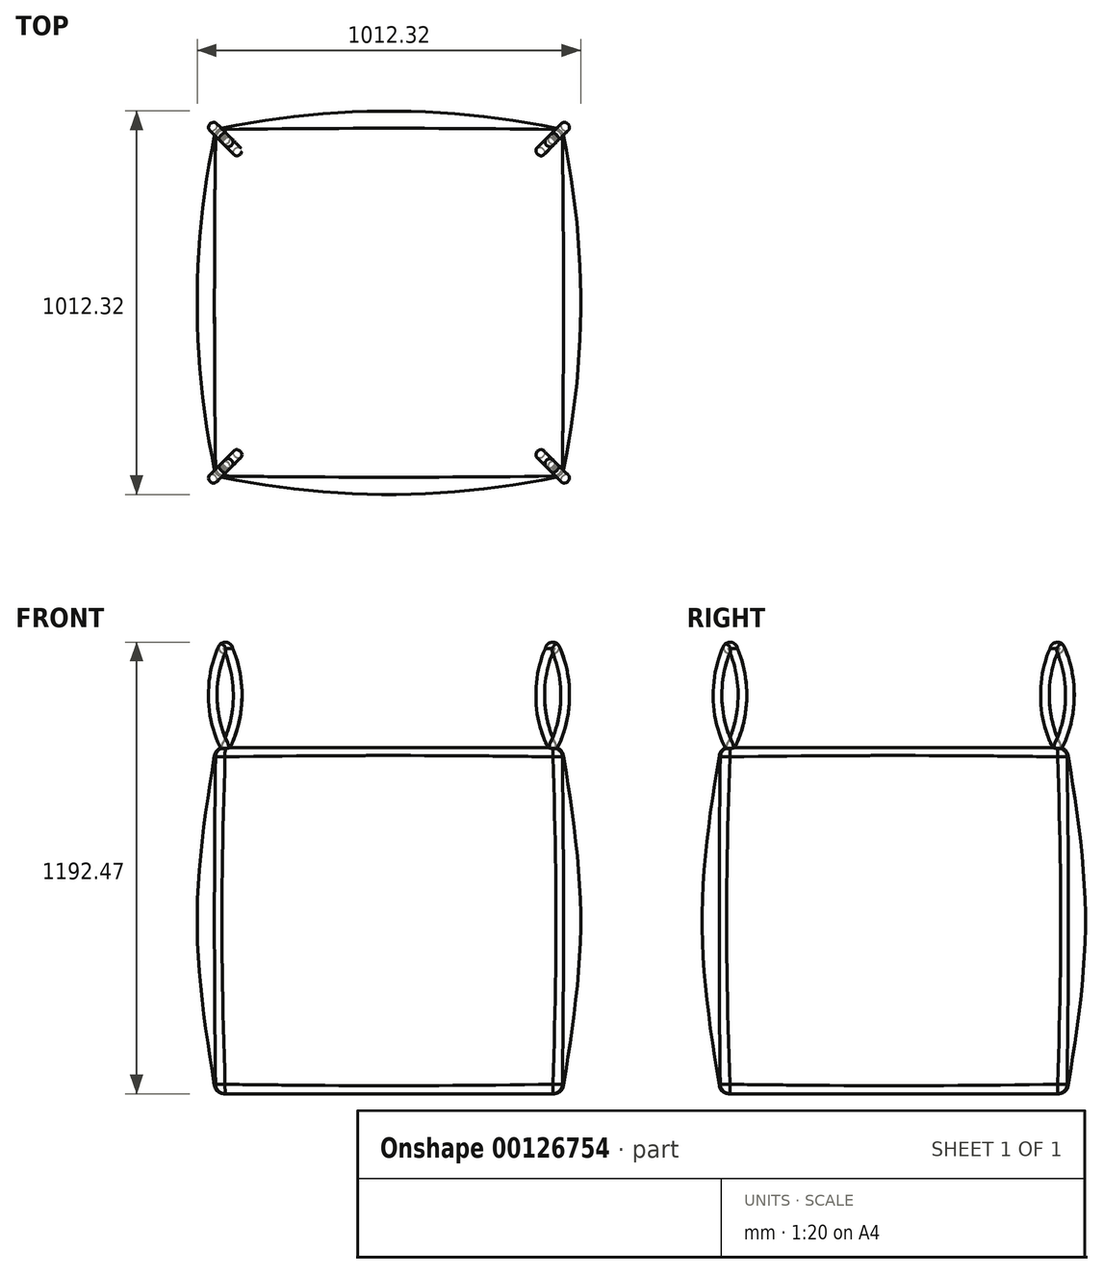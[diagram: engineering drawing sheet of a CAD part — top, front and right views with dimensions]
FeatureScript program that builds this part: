
annotation { "Feature Type Name" : "Feature", "Feature Type Description" : "" }
export const myFeature = defineFeature(function(context is Context, id is Id, definition is map)
    precondition{}
    {
        {
            var Q0;
            Q0=qCreatedBy(makeId("Top.planeOp"),FACE);
            var sketch = newSketch(context, id + "F0", { "sketchPlane" : qUnion([Q0])});
            skLineSegment(sketch, "E0.bottom", {"start": v(457.2, 457.2) * mm, "end": v(-457.2, 457.2) * mm});
            skLineSegment(sketch, "E0.top", {"start": v(457.2, -457.2) * mm, "end": v(-457.2, -457.2) * mm});
            skLineSegment(sketch, "E0.left", {"start": v(457.2, 457.2) * mm, "end": v(457.2, -457.2) * mm});
            skLineSegment(sketch, "E0.right", {"start": v(-457.2, 457.2) * mm, "end": v(-457.2, -457.2) * mm});
            skPoint(sketch, "E0.middle", {"position": v(0, 0) * mm});
            skSolve(sketch);
        }
        {
            var Q0;
            Q0=qCreatedBy(makeId("Top.planeOp"),FACE);
            cPlane(context, id + "F1", {"entities" : qUnion([Q0]), "cplaneType" : CPlaneType.OFFSET, "offset" : 457.2 * mm, "width" : 152.4 * mm, "height" : 152.4 * mm});
        }
        {
            var Q0;
            Q0=qCreatedBy(makeId("Top.planeOp"),FACE);
            cPlane(context, id + "F2", {"entities" : qUnion([Q0]), "cplaneType" : CPlaneType.OFFSET, "offset" : 914.4 * mm, "width" : 152.4 * mm, "height" : 152.4 * mm});
        }
        {
            var Q0;
            Q0=qCreatedBy(id+"F1.planeOp",FACE);
            var sketch = newSketch(context, id + "F3", { "sketchPlane" : qUnion([Q0])});
            skLineSegment(sketch, "E1.0", {"start": v(457.2, 457.2) * mm, "end": v(-457.2, 457.2) * mm, "construction": true});
            skLineSegment(sketch, "E2.0", {"start": v(-457.2, 457.2) * mm, "end": v(-457.2, -457.2) * mm, "construction": true});
            skLineSegment(sketch, "E3.0", {"start": v(457.2, -457.2) * mm, "end": v(-457.2, -457.2) * mm, "construction": true});
            skLineSegment(sketch, "E4.0", {"start": v(457.2, 457.2) * mm, "end": v(457.2, -457.2) * mm, "construction": true});
            skArc(sketch, "E5", {"start": v(457.2, 457.2) * mm, "mid": v(0, 506.16) * mm, "end": v(-457.2, 457.2) * mm});
            skArc(sketch, "E6", {"start": v(457.2, -457.2) * mm, "mid": v(506.16, 0) * mm, "end": v(457.2, 457.2) * mm});
            skArc(sketch, "E7", {"start": v(-457.2, -457.2) * mm, "mid": v(0, -506.16) * mm, "end": v(457.2, -457.2) * mm});
            skArc(sketch, "E8", {"start": v(-457.2, 457.2) * mm, "mid": v(-506.16, 0) * mm, "end": v(-457.2, -457.2) * mm});
            skSolve(sketch);
        }
        {
            var Q0;
            Q0=qCreatedBy(id+"F2.planeOp",FACE);
            var sketch = newSketch(context, id + "F4", { "sketchPlane" : qUnion([Q0])});
            skLineSegment(sketch, "E9.0.0", {"start": v(457.2, -457.2) * mm, "end": v(457.2, 457.2) * mm});
            skLineSegment(sketch, "E9.0.1", {"start": v(457.2, 457.2) * mm, "end": v(-457.2, 457.2) * mm});
            skLineSegment(sketch, "E9.0.2", {"start": v(-457.2, 457.2) * mm, "end": v(-457.2, -457.2) * mm});
            skLineSegment(sketch, "E9.0.3", {"start": v(-457.2, -457.2) * mm, "end": v(457.2, -457.2) * mm});
            skSolve(sketch);
        }
        {
            var Q0;
            Q0=makeQuery(id+"F0.imprint","IMPRINT",FACE,{"disambiguationData":[TD([[makeQuery(id+"F0.imprint","IMPRINT",EDGE,{"derivedFrom":sQuery(id+"F0.wireOp",EDGE,"E0.bottom")}),1.0]])]});
            var Q1;
            Q1=makeQuery(id+"F3.imprint","IMPRINT",FACE,{"disambiguationData":[TD([[makeQuery(id+"F3.imprint","IMPRINT",EDGE,{"derivedFrom":sQuery(id+"F3.wireOp",EDGE,"E5")}),1.0]])]});
            var Q2;
            Q2=makeQuery(id+"F4.imprint","IMPRINT",FACE,{"disambiguationData":[TD([[makeQuery(id+"F4.imprint","IMPRINT",EDGE,{"derivedFrom":sQuery(id+"F4.wireOp",EDGE,"E9.0.0")}),1.0]])]});
            loft(context, id + "F5", {"sheetProfilesArray" : [{ "sheetProfileEntities" : qUnion([Q0]) }, { "sheetProfileEntities" : qUnion([Q1]) }, { "sheetProfileEntities" : qUnion([Q2]) }]});
        }
        {
            var Q0;
            Q0=makeQuery(id+"F5.opLoft","CAP_FACE",FACE,{"disambiguationData":[OSD([makeQuery(id+"F4.imprint","IMPRINT",FACE,{"disambiguationData":[TD([[makeQuery(id+"F4.imprint","IMPRINT",EDGE,{"derivedFrom":sQuery(id+"F4.wireOp",EDGE,"E9.0.0")}),1.0]])]})])],"isStart":true});
            var Q1;
            Q1=makeQuery(id+"F5.opLoft","CAP_FACE",FACE,{"disambiguationData":[OSD([makeQuery(id+"F0.imprint","IMPRINT",FACE,{"disambiguationData":[TD([[makeQuery(id+"F0.imprint","IMPRINT",EDGE,{"derivedFrom":sQuery(id+"F0.wireOp",EDGE,"E0.bottom")}),1.0]])]})])],"isStart":true});
            var Q2;
            Q2=makeQuery(id+"F5.opLoft","SWEPT_EDGE",EDGE,{"disambiguationData":[OSD([sQuery(id+"F0.wireOp",EDGE,"E0.top"),sQuery(id+"F0.wireOp",EDGE,"E0.left"),sQuery(id+"F3.wireOp",EDGE,"E6"),sQuery(id+"F3.wireOp",EDGE,"E7")])]});
            var Q3;
            Q3=makeQuery(id+"F5.opLoft","SWEPT_EDGE",EDGE,{"disambiguationData":[OSD([sQuery(id+"F3.wireOp",EDGE,"E6"),sQuery(id+"F3.wireOp",EDGE,"E7"),sQuery(id+"F4.wireOp",EDGE,"E9.0.0"),sQuery(id+"F4.wireOp",EDGE,"E9.0.3")])]});
            var Q4;
            Q4=makeQuery(id+"F5.opLoft","SWEPT_EDGE",EDGE,{"disambiguationData":[OSD([sQuery(id+"F0.wireOp",EDGE,"E0.bottom"),sQuery(id+"F0.wireOp",EDGE,"E0.left"),sQuery(id+"F3.wireOp",EDGE,"E5"),sQuery(id+"F3.wireOp",EDGE,"E6")])]});
            var Q5;
            Q5=makeQuery(id+"F5.opLoft","SWEPT_EDGE",EDGE,{"disambiguationData":[OSD([sQuery(id+"F3.wireOp",EDGE,"E5"),sQuery(id+"F3.wireOp",EDGE,"E6"),sQuery(id+"F4.wireOp",EDGE,"E9.0.0"),sQuery(id+"F4.wireOp",EDGE,"E9.0.1")])]});
            var Q6;
            Q6=makeQuery(id+"F5.opLoft","SWEPT_FACE",FACE,{"disambiguationData":[OSD([sQuery(id+"F0.wireOp",EDGE,"E0.bottom"),sQuery(id+"F0.wireOp",EDGE,"E0.top"),sQuery(id+"F0.wireOp",EDGE,"E0.right"),sQuery(id+"F3.wireOp",EDGE,"E5"),sQuery(id+"F3.wireOp",EDGE,"E7"),sQuery(id+"F3.wireOp",EDGE,"E8")])]});
            fillet(context, id + "F6", {"entities" : qUnion([Q0, Q1, Q2, Q3, Q4, Q5, Q6]), "radius" : 25.4 * mm, "tangentPropagation" : true, "allowEdgeOverflow" : false});
        }
        {
            var Q0;
            {var subQ0=sQuery(id+"F4.wireOp",EDGE,"E9.0.0");var subQ1=sQuery(id+"F4.wireOp",EDGE,"E9.0.1");var subQ2=sQuery(id+"F4.wireOp",EDGE,"E9.0.2");var subQ3=sQuery(id+"F4.wireOp",EDGE,"E9.0.3");Q0=makeQuery(id+"F6.opFillet","BLEND_VERTEX",VERTEX,{"blendedFrom":[makeQuery(id+"F5.opLoft","MID_CAP_VERTEX",VERTEX,{"disambiguationData":[OSD([subQ2,subQ3])],"capPos":2.0}),makeQuery(id+"F5.opLoft","MID_CAP_EDGE",EDGE,{"disambiguationData":[OSD([subQ0,subQ2,subQ3])],"capPos":2.0}),makeQuery(id+"F5.opLoft","MID_CAP_EDGE",EDGE,{"disambiguationData":[OSD([subQ1,subQ2,subQ3])],"capPos":2.0}),makeQuery(id+"F5.opLoft","CAP_FACE",FACE,{"disambiguationData":[OSD([makeQuery(id+"F4.imprint","IMPRINT",FACE,{"disambiguationData":[TD([[makeQuery(id+"F4.imprint","IMPRINT",EDGE,{"derivedFrom":subQ0}),1.0]])]})])],"isStart":true})],"blendedInto":[makeQuery(id+"F5.opLoft","CAP_FACE",FACE,{"disambiguationData":[OSD([makeQuery(id+"F4.imprint","IMPRINT",FACE,{"disambiguationData":[TD([[makeQuery(id+"F4.imprint","IMPRINT",EDGE,{"derivedFrom":subQ0}),1.0]])]})])],"isStart":true})]});}
            var Q1;
            {var subQ0=sQuery(id+"F4.wireOp",EDGE,"E9.0.0");var subQ1=sQuery(id+"F4.wireOp",EDGE,"E9.0.1");var subQ2=sQuery(id+"F4.wireOp",EDGE,"E9.0.2");var subQ3=sQuery(id+"F4.wireOp",EDGE,"E9.0.3");Q1=makeQuery(id+"F6.opFillet","BLEND_VERTEX",VERTEX,{"blendedFrom":[makeQuery(id+"F5.opLoft","MID_CAP_VERTEX",VERTEX,{"disambiguationData":[OSD([subQ0,subQ1])],"capPos":2.0}),makeQuery(id+"F5.opLoft","MID_CAP_EDGE",EDGE,{"disambiguationData":[OSD([subQ0,subQ1,subQ3])],"capPos":2.0}),makeQuery(id+"F5.opLoft","MID_CAP_EDGE",EDGE,{"disambiguationData":[OSD([subQ0,subQ1,subQ2])],"capPos":2.0}),makeQuery(id+"F5.opLoft","CAP_FACE",FACE,{"disambiguationData":[OSD([makeQuery(id+"F4.imprint","IMPRINT",FACE,{"disambiguationData":[TD([[makeQuery(id+"F4.imprint","IMPRINT",EDGE,{"derivedFrom":subQ0}),1.0]])]})])],"isStart":true})],"blendedInto":[makeQuery(id+"F5.opLoft","CAP_FACE",FACE,{"disambiguationData":[OSD([makeQuery(id+"F4.imprint","IMPRINT",FACE,{"disambiguationData":[TD([[makeQuery(id+"F4.imprint","IMPRINT",EDGE,{"derivedFrom":subQ0}),1.0]])]})])],"isStart":true})]});}
            var Q2;
            {var subQ0=sQuery(id+"F0.wireOp",EDGE,"E0.bottom");var subQ1=sQuery(id+"F0.wireOp",EDGE,"E0.top");var subQ2=sQuery(id+"F0.wireOp",EDGE,"E0.left");var subQ3=sQuery(id+"F0.wireOp",EDGE,"E0.right");Q2=makeQuery(id+"F6.opFillet","BLEND_VERTEX",VERTEX,{"blendedFrom":[makeQuery(id+"F5.opLoft","MID_CAP_VERTEX",VERTEX,{"disambiguationData":[OSD([subQ0,subQ2])],"capPos":0.0}),makeQuery(id+"F5.opLoft","MID_CAP_EDGE",EDGE,{"disambiguationData":[OSD([subQ0,subQ2,subQ3])],"capPos":0.0}),makeQuery(id+"F5.opLoft","MID_CAP_EDGE",EDGE,{"disambiguationData":[OSD([subQ0,subQ1,subQ2])],"capPos":0.0}),makeQuery(id+"F5.opLoft","CAP_FACE",FACE,{"disambiguationData":[OSD([makeQuery(id+"F0.imprint","IMPRINT",FACE,{"disambiguationData":[TD([[makeQuery(id+"F0.imprint","IMPRINT",EDGE,{"derivedFrom":subQ0}),1.0]])]})])],"isStart":true})],"blendedInto":[makeQuery(id+"F5.opLoft","CAP_FACE",FACE,{"disambiguationData":[OSD([makeQuery(id+"F0.imprint","IMPRINT",FACE,{"disambiguationData":[TD([[makeQuery(id+"F0.imprint","IMPRINT",EDGE,{"derivedFrom":subQ0}),1.0]])]})])],"isStart":true})]});}
            cPlane(context, id + "F7", {"entities" : qUnion([Q0, Q1, Q2]), "cplaneType" : CPlaneType.THREE_POINT, "offset" : 25.4 * mm, "width" : 152.4 * mm, "height" : 152.4 * mm});
        }
        {
            var Q0;
            Q0=qCreatedBy(id+"F7.planeOp",FACE);
            var sketch = newSketch(context, id + "F8", { "sketchPlane" : qUnion([Q0])});
            skFitSpline(sketch, "E10.0", {"points": [v(611.26, 914.4) * mm, v(407.5, 914.4) * mm, v(203.75, 914.4) * mm, v(0, 914.4) * mm], "construction": true});
            skLineSegment(sketch, "E11", {"start": v(611.26, 914.4) * mm, "end": v(611.26, 1168.4) * mm, "construction": true});
            skArc(sketch, "E12", {"start": v(611.26, 914.4) * mm, "mid": v(657.5, 1043.13) * mm, "end": v(621.97, 1175.22) * mm});
            skArc(sketch, "E13", {"start": v(600.54, 1175.22) * mm, "mid": v(565.01, 1043.13) * mm, "end": v(611.26, 914.4) * mm});
            skPoint(sketch, "E14.visualSharp", {"position": v(611.26, 1168.4) * mm});
            skArc(sketch, "E14.filletArc", {"start": v(621.97, 1175.22) * mm, "mid": v(611.26, 1181.1) * mm, "end": v(600.54, 1175.22) * mm});
            skLineSegment(sketch, "E15", {"start": v(0, 914.4) * mm, "end": v(0, 1050.27) * mm, "construction": true});
            skSolve(sketch);
        }
        {
            var Q0;
            Q0=makeQuery(id+"F5.opLoft","CAP_FACE",FACE,{"disambiguationData":[OSD([makeQuery(id+"F4.imprint","IMPRINT",FACE,{"disambiguationData":[TD([[makeQuery(id+"F4.imprint","IMPRINT",EDGE,{"derivedFrom":sQuery(id+"F4.wireOp",EDGE,"E9.0.0")}),1.0]])]})])],"isStart":true});
            var sketch = newSketch(context, id + "F9", { "sketchPlane" : qUnion([Q0])});
            skCircle(sketch, "E16", {"center": v(432.23, 432.23) * mm, "radius": 12.7 * mm});
            skSolve(sketch);
        }
        {
            var Q0;
            Q0 = qSketchRegion(id + "F9", true);
            var Q1;
            Q1 = qConstructionFilter(qBodyType(qCreatedBy(id + "F8" ,EDGE), BodyType.WIRE), ConstructionObject.NO);
            sweep(context, id + "F10", {"operationType" : NewBodyOperationType.ADD, "profiles" : qUnion([Q0]), "path" : qUnion([Q1])});
        }
        {
            var Q0;
            Q0=makeQuery(id+"F5.opLoft","SWEPT_BODY",BODY,{"disambiguationData":[OSD([makeQuery(id+"F0.imprint","IMPRINT",FACE,{"disambiguationData":[TD([[makeQuery(id+"F0.imprint","IMPRINT",EDGE,{"derivedFrom":sQuery(id+"F0.wireOp",EDGE,"E0.bottom")}),1.0]])]}),sQuery(id+"F3.wireOp",EDGE,"E8"),makeQuery(id+"F4.imprint","IMPRINT",FACE,{"disambiguationData":[TD([[makeQuery(id+"F4.imprint","IMPRINT",EDGE,{"derivedFrom":sQuery(id+"F4.wireOp",EDGE,"E9.0.0")}),1.0]])]})])]});
            var Q1;
            Q1=sQuery(id+"F8.wireOp",EDGE,"E15");
            circularPattern(context, id + "F11", {"entities" : qUnion([Q0]), "axis" : qUnion([Q1]), "angle" : 360 * degree, "instanceCount" : 4, "equalSpace" : true});
        }
        {
            var Q0;
            Q0=makeQuery(id+"F5.opLoft","SWEPT_BODY",BODY,{"disambiguationData":[OSD([makeQuery(id+"F0.imprint","IMPRINT",FACE,{"disambiguationData":[TD([[makeQuery(id+"F0.imprint","IMPRINT",EDGE,{"derivedFrom":sQuery(id+"F0.wireOp",EDGE,"E0.bottom")}),1.0]])]}),sQuery(id+"F3.wireOp",EDGE,"E8"),makeQuery(id+"F4.imprint","IMPRINT",FACE,{"disambiguationData":[TD([[makeQuery(id+"F4.imprint","IMPRINT",EDGE,{"derivedFrom":sQuery(id+"F4.wireOp",EDGE,"E9.0.0")}),1.0]])]})])]});
            transform(context, id + "F12", {"entities" : qUnion([Q0]), "transformType" : TransformType.TRANSLATION_3D, "dx" : 0 * mm, "dy" : 0 * mm, "dz" : 0 * mm, "makeCopy" : true});
        }
        {
            var Q0;
            Q0=makeQuery(id+"F12.opPattern","COPY",BODY,{"derivedFrom":makeQuery(id+"F5.opLoft","SWEPT_BODY",BODY,{"disambiguationData":[OSD([makeQuery(id+"F0.imprint","IMPRINT",FACE,{"disambiguationData":[TD([[makeQuery(id+"F0.imprint","IMPRINT",EDGE,{"derivedFrom":sQuery(id+"F0.wireOp",EDGE,"E0.bottom")}),1.0]])]}),sQuery(id+"F3.wireOp",EDGE,"E8"),makeQuery(id+"F4.imprint","IMPRINT",FACE,{"disambiguationData":[TD([[makeQuery(id+"F4.imprint","IMPRINT",EDGE,{"derivedFrom":sQuery(id+"F4.wireOp",EDGE,"E9.0.0")}),1.0]])]})])]}),"instanceName":"1"});
            deleteBodies(context, id + "F13", {"entities" : qUnion([Q0])});
        }
    });
